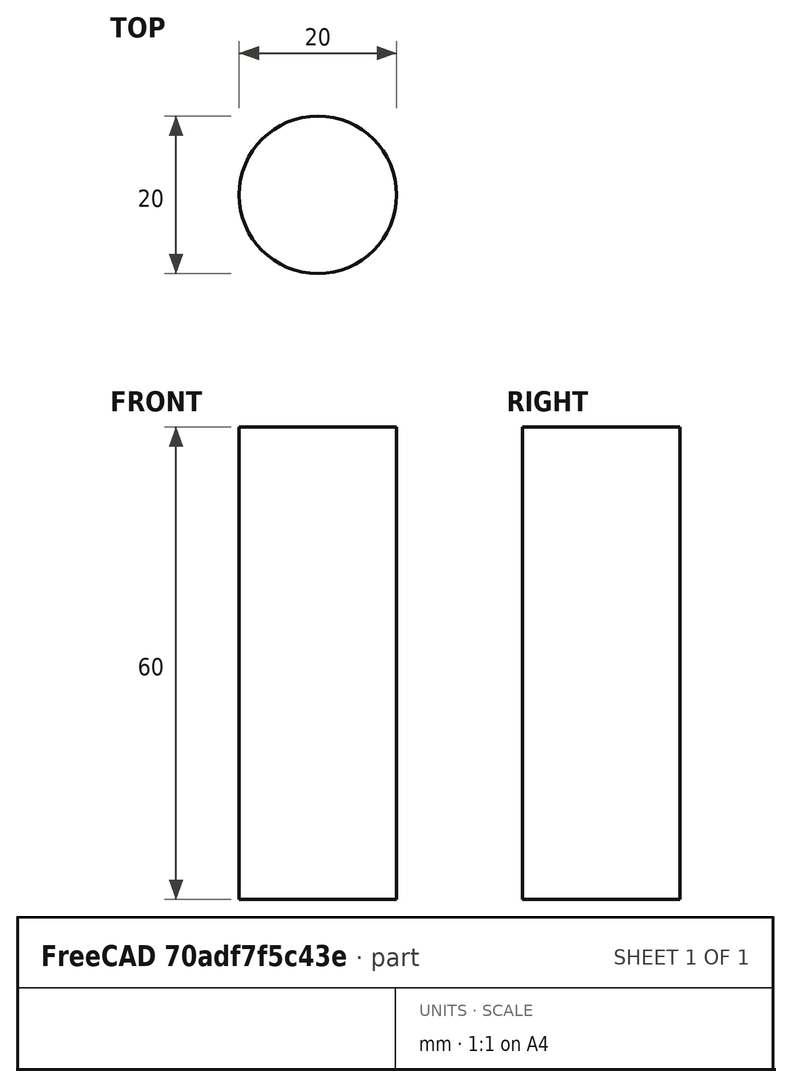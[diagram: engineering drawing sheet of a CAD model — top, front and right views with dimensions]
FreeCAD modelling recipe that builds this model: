
FCSTD DOCUMENT  (FreeCAD 0.20R29177 (Git))
Label: IntestineV1_outer_collision
License: All rights reserved
LicenseURL: http://en.wikipedia.org/wiki/All_rights_reserved
objects: Sketcher::SketchObject×1, Part::Revolution×1, Part::Reverse×1
note: 3 computed .brp shape members not serialized (recipe doc carries the construction recipe); baked Part::Feature solids carry a one-line shape summary decoded from their .brp

FEATURE [Sketcher::SketchObject] Sketch
  FullyConstrained = true
  Placement = pos=(0,0,0) rot=(1,0,0;1.5708rad)
  sketch-geometry (1):
    g0: LineSegment StartX=10 StartY=60 StartZ=0 EndX=10 EndY=0 EndZ=0
  constraints (4):
    c: Vertical(g0)
    c: DistanceX(g-1,g0) = 10
    c: DistanceY(g0,g-1) = 0
    c: DistanceY(g0,g0) = 60
FEATURE [Part::Revolution] Revolve
  Angle = 360
  Axis = (0,0,1)
  Base = (0,0,0)
  FaceMakerClass = Part::FaceMakerBullseye
  Solid = false
  Source = -> Sketch
  Symmetric = false
FEATURE [Part::Reverse] Revolve_rev  label="Revolve (Rev)"
  Source = -> Revolve
